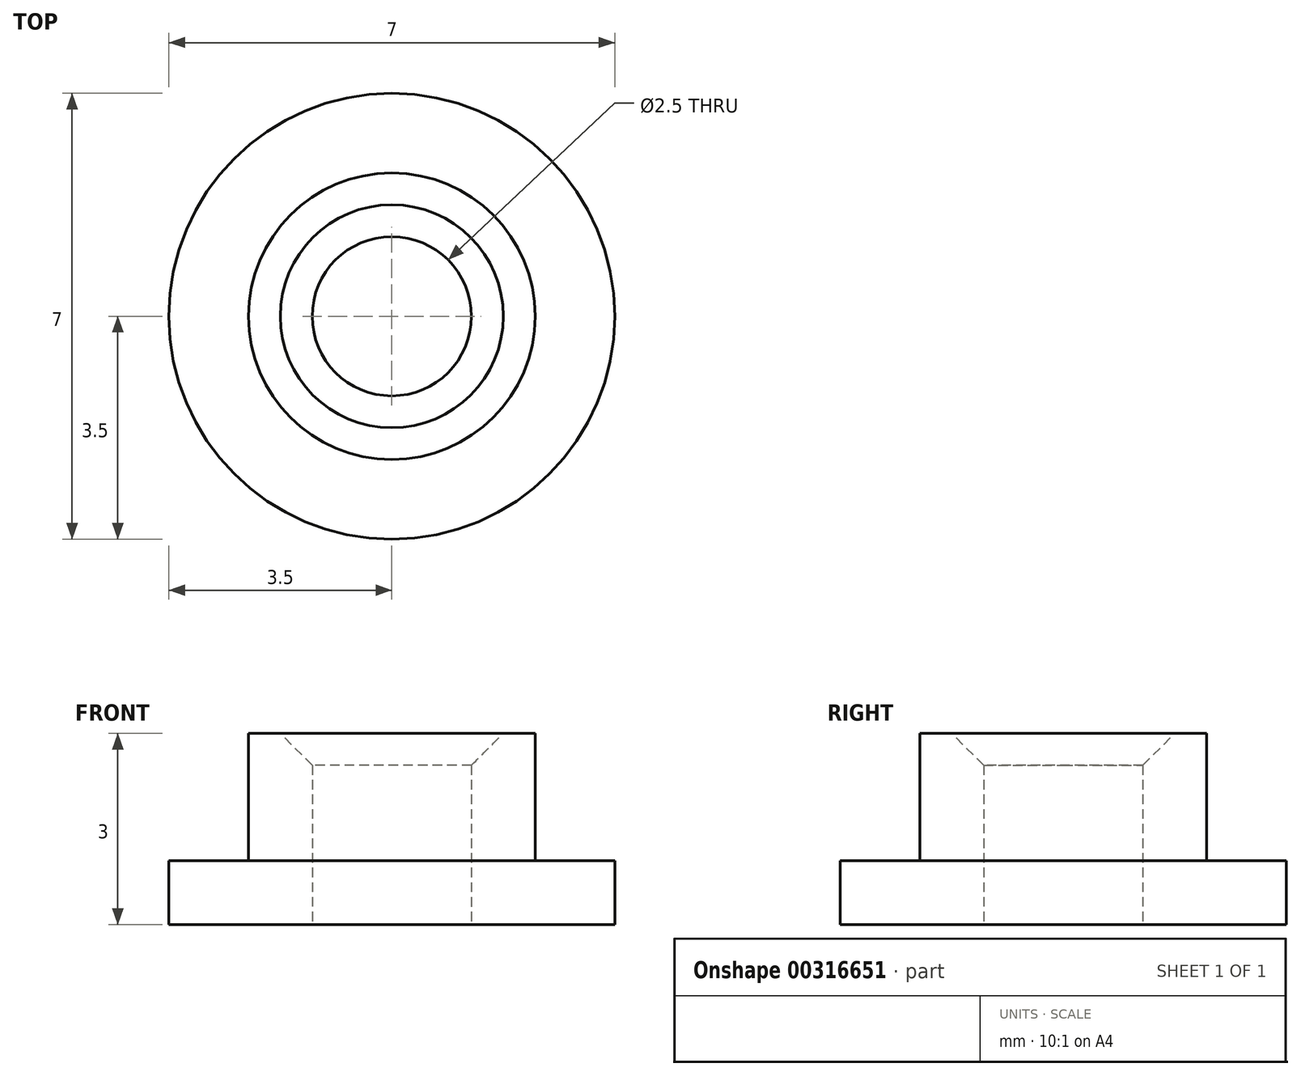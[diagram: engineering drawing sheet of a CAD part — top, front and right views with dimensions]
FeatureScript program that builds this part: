
annotation { "Feature Type Name" : "Feature", "Feature Type Description" : "" }
export const myFeature = defineFeature(function(context is Context, id is Id, definition is map)
    precondition{}
    {
        {
            var Q0;
            Q0=qCreatedBy(makeId("Top.planeOp"),FACE);
            var sketch = newSketch(context, id + "F0", { "sketchPlane" : qUnion([Q0])});
            skCircle(sketch, "E0", {"center": v(0, 0) * mm, "radius": 2.25 * mm});
            skCircle(sketch, "E1", {"center": v(0, 0) * mm, "radius": 1.25 * mm});
            skSolve(sketch);
        }
        {
            var Q0;
            Q0=makeQuery(id+"F0.imprint","IMPRINT",FACE,{"disambiguationData":[TD([[makeQuery(id+"F0.imprint","IMPRINT",EDGE,{"derivedFrom":sQuery(id+"F0.wireOp",EDGE,"E0")}),1.0]])]});
            extrude(context, id + "F1", {"entities" : qUnion([Q0]), "depth" : 2 * mm});
        }
        {
            var Q0;
            Q0=makeQuery(id+"F1.opExtrude","CAP_EDGE",EDGE,{"disambiguationData":[OSD([sQuery(id+"F0.wireOp",EDGE,"E1")])],"isStart":false});
            chamfer(context, id + "F2", {"entities" : qUnion([Q0]), "width" : 0.5 * mm, "tangentPropagation" : true});
        }
        {
            var Q0;
            Q0=makeQuery(id+"F1.opExtrude","CAP_FACE",FACE,{"disambiguationData":[OSD([sQuery(id+"F0.wireOp",EDGE,"E0"),sQuery(id+"F0.wireOp",EDGE,"E1")])],"isStart":true});
            var sketch = newSketch(context, id + "F3", { "sketchPlane" : qUnion([Q0])});
            skCircle(sketch, "E2", {"center": v(0, 0) * mm, "radius": 3.5 * mm});
            skCircle(sketch, "E3.0", {"center": v(0, 0) * mm, "radius": 1.25 * mm});
            skSolve(sketch);
        }
        {
            var Q0;
            Q0 = qSketchRegion(id + "F3", true);
            extrude(context, id + "F4", {"entities" : qUnion([Q0]), "operationType" : NewBodyOperationType.ADD, "depth" : 1 * mm});
        }
    });
